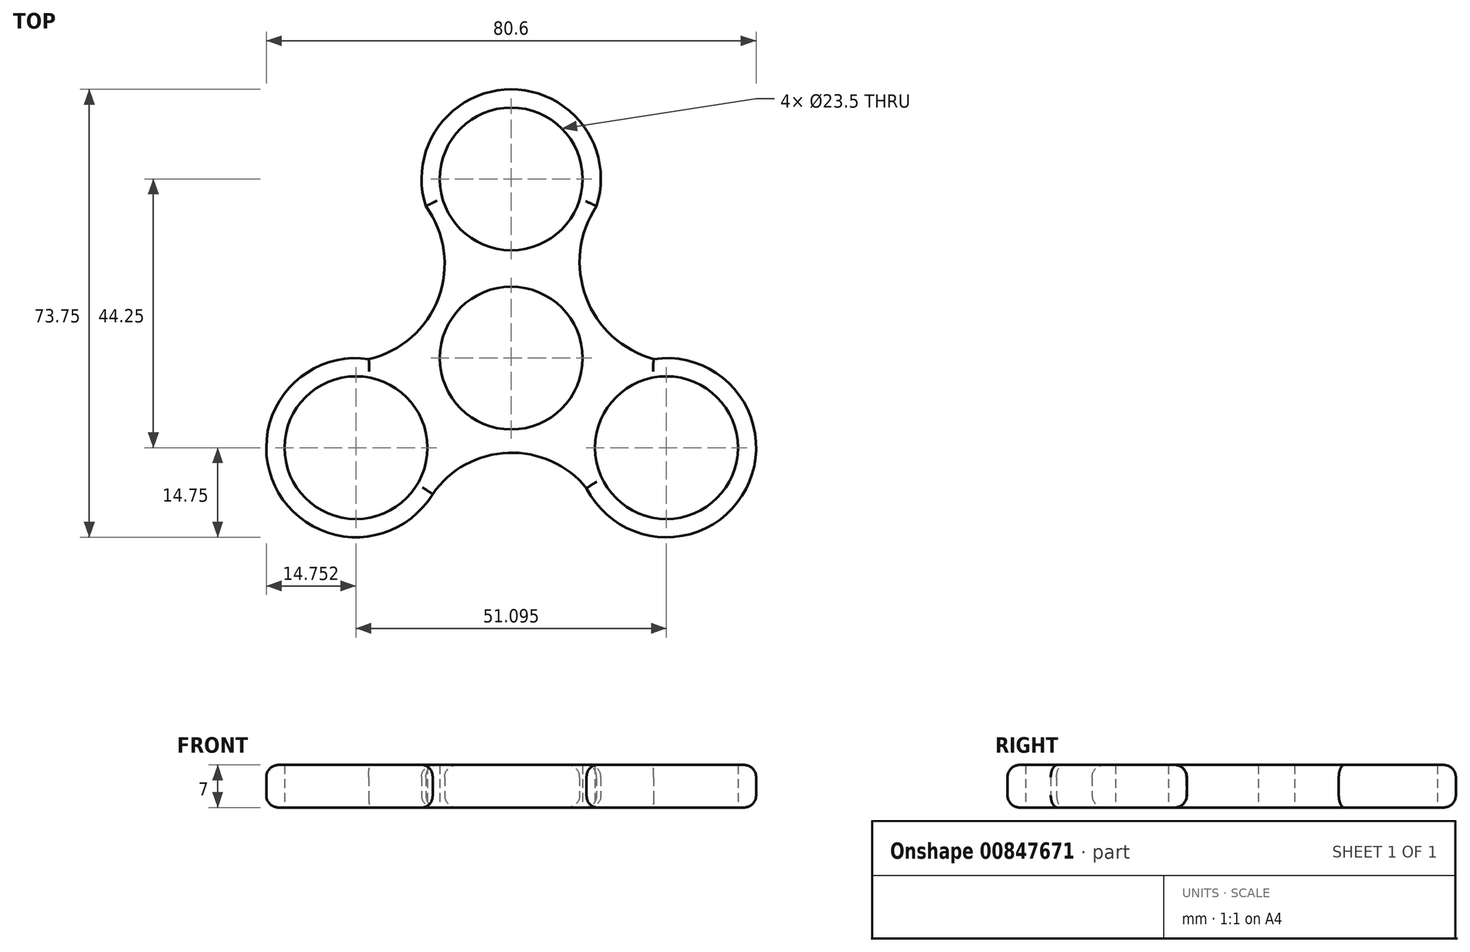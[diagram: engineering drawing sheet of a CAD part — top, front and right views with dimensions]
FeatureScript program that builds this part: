
annotation { "Feature Type Name" : "Feature", "Feature Type Description" : "" }
export const myFeature = defineFeature(function(context is Context, id is Id, definition is map)
    precondition{}
    {
        {
            var Q0;
            Q0=qCreatedBy(makeId("Top.planeOp"),FACE);
            var sketch = newSketch(context, id + "F0", { "sketchPlane" : qUnion([Q0])});
            skCircle(sketch, "E0", {"center": v(0, 0) * mm, "radius": 14.75 * mm});
            skLineSegment(sketch, "E1", {"start": v(0, 0) * mm, "end": v(0, 29.5) * mm});
            skCircle(sketch, "E2", {"center": v(0, 29.5) * mm, "radius": 14.75 * mm});
            skCircle(sketch, "E3", {"center": v(0, 29.5) * mm, "radius": 11.75 * mm});
            skCircle(sketch, "E4", {"center": v(0, 0) * mm, "radius": 11.75 * mm});
            skCircle(sketch, "E5.1.0", {"center": v(-25.55, -14.75) * mm, "radius": 14.75 * mm});
            skCircle(sketch, "E5.1.1", {"center": v(-25.55, -14.75) * mm, "radius": 11.75 * mm});
            skCircle(sketch, "E5.2.0", {"center": v(25.55, -14.75) * mm, "radius": 14.75 * mm});
            skCircle(sketch, "E5.2.1", {"center": v(25.55, -14.75) * mm, "radius": 11.75 * mm});
            skArc(sketch, "E6", {"start": v(14.05, 25) * mm, "mid": v(12.3, 10.03) * mm, "end": v(23.42, -0.15) * mm});
            skArc(sketch, "E7", {"start": v(-23.42, -0.15) * mm, "mid": v(-11.96, 9.9) * mm, "end": v(-14.05, 25) * mm});
            skArc(sketch, "E8", {"start": v(12.4, -21.43) * mm, "mid": v(-0.5, -15.6) * mm, "end": v(-12.93, -22.39) * mm});
            skSolve(sketch);
        }
        {
            var Q0;
            {var subQ0=sQuery(id+"F0.wireOp",EDGE,"E5.1.0");var subQ1=sQuery(id+"F0.wireOp",EDGE,"E0");var subQ2=makeQuery(id+"F0.imprint","INTERSECT",VERTEX,{"derivedFrom":[subQ1,subQ0]});Q0=makeQuery(id+"F0.imprint","IMPRINT",FACE,{"disambiguationData":[TD([[makeQuery(id+"F0.imprint","IMPRINT",EDGE,{"disambiguationData":[TD([[subQ2,1.0]])],"derivedFrom":subQ1}),-1.0]])]});}
            var Q1;
            Q1=makeQuery(id+"F0.imprint","IMPRINT",FACE,{"disambiguationData":[TD([[makeQuery(id+"F0.imprint","IMPRINT",EDGE,{"derivedFrom":sQuery(id+"F0.wireOp",EDGE,"E3")}),-1.0]])]});
            var Q2;
            {var subQ0=sQuery(id+"F0.wireOp",EDGE,"E2");var subQ1=sQuery(id+"F0.wireOp",EDGE,"E0");var subQ2=makeQuery(id+"F0.imprint","INTERSECT",VERTEX,{"derivedFrom":[subQ1,subQ0]});Q2=makeQuery(id+"F0.imprint","IMPRINT",FACE,{"disambiguationData":[TD([[makeQuery(id+"F0.imprint","IMPRINT",EDGE,{"disambiguationData":[TD([[subQ2,1.0]])],"derivedFrom":subQ1}),-1.0]])]});}
            var Q3;
            {var subQ5=sQuery(id+"F0.wireOp",EDGE,"E8");Q3=makeQuery(id+"F0.imprint","IMPRINT",FACE,{"disambiguationData":[TD([[makeQuery(id+"F0.imprint","IMPRINT",EDGE,{"derivedFrom":subQ5}),-1.0]])]});}
            var Q4;
            Q4=makeQuery(id+"F0.imprint","IMPRINT",FACE,{"disambiguationData":[TD([[makeQuery(id+"F0.imprint","IMPRINT",EDGE,{"derivedFrom":sQuery(id+"F0.wireOp",EDGE,"E5.2.1")}),-1.0]])]});
            var Q5;
            Q5=makeQuery(id+"F0.imprint","IMPRINT",FACE,{"disambiguationData":[TD([[makeQuery(id+"F0.imprint","IMPRINT",EDGE,{"derivedFrom":sQuery(id+"F0.wireOp",EDGE,"E4")}),-1.0]])]});
            var Q6;
            Q6=makeQuery(id+"F0.imprint","IMPRINT",FACE,{"disambiguationData":[TD([[makeQuery(id+"F0.imprint","IMPRINT",EDGE,{"derivedFrom":sQuery(id+"F0.wireOp",EDGE,"E5.1.1")}),-1.0]])]});
            extrude(context, id + "F1", {"entities" : qUnion([Q0, Q1, Q2, Q3, Q4, Q5, Q6]), "depth" : 7 * mm, "offsetDistance" : 25 * mm});
        }
        {
            var Q0;
            Q0=makeQuery(id+"F1.opExtrude","CAP_EDGE",EDGE,{"disambiguationData":[OSD([sQuery(id+"F0.wireOp",EDGE,"E2")])],"isStart":false});
            var Q1;
            Q1=makeQuery(id+"F1.opExtrude","CAP_EDGE",EDGE,{"disambiguationData":[OSD([sQuery(id+"F0.wireOp",EDGE,"E6")])],"isStart":false});
            var Q2;
            Q2=makeQuery(id+"F1.opExtrude","CAP_EDGE",EDGE,{"disambiguationData":[OSD([sQuery(id+"F0.wireOp",EDGE,"E5.2.0")])],"isStart":false});
            var Q3;
            Q3=makeQuery(id+"F1.opExtrude","CAP_EDGE",EDGE,{"disambiguationData":[OSD([sQuery(id+"F0.wireOp",EDGE,"E8")])],"isStart":false});
            var Q4;
            Q4=makeQuery(id+"F1.opExtrude","CAP_EDGE",EDGE,{"disambiguationData":[OSD([sQuery(id+"F0.wireOp",EDGE,"E5.1.0")])],"isStart":false});
            var Q5;
            Q5=makeQuery(id+"F1.opExtrude","CAP_EDGE",EDGE,{"disambiguationData":[OSD([sQuery(id+"F0.wireOp",EDGE,"E7")])],"isStart":false});
            var Q6;
            Q6=makeQuery(id+"F1.opExtrude","CAP_EDGE",EDGE,{"disambiguationData":[OSD([sQuery(id+"F0.wireOp",EDGE,"E2")])],"isStart":true});
            var Q7;
            Q7=makeQuery(id+"F1.opExtrude","CAP_EDGE",EDGE,{"disambiguationData":[OSD([sQuery(id+"F0.wireOp",EDGE,"E7")])],"isStart":true});
            var Q8;
            Q8=makeQuery(id+"F1.opExtrude","CAP_EDGE",EDGE,{"disambiguationData":[OSD([sQuery(id+"F0.wireOp",EDGE,"E6")])],"isStart":true});
            var Q9;
            Q9=makeQuery(id+"F1.opExtrude","CAP_EDGE",EDGE,{"disambiguationData":[OSD([sQuery(id+"F0.wireOp",EDGE,"E5.2.0")])],"isStart":true});
            var Q10;
            Q10=makeQuery(id+"F1.opExtrude","CAP_EDGE",EDGE,{"disambiguationData":[OSD([sQuery(id+"F0.wireOp",EDGE,"E8")])],"isStart":true});
            var Q11;
            Q11=makeQuery(id+"F1.opExtrude","CAP_EDGE",EDGE,{"disambiguationData":[OSD([sQuery(id+"F0.wireOp",EDGE,"E5.1.0")])],"isStart":true});
            fillet(context, id + "F2", {"entities" : qUnion([Q0, Q1, Q2, Q3, Q4, Q5, Q6, Q7, Q8, Q9, Q10, Q11]), "radius" : 2 * mm, "tangentPropagation" : true, "allowEdgeOverflow" : false});
        }
    });
